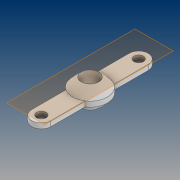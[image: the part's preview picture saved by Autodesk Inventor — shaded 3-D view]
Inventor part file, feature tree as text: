
AUTODESK INVENTOR PART (.ipt)
format: ipt  version: 2021 (Build 250183000, 183)  size: 140,288 bytes
history: native  units: mm
features: sketch x4, extrude x2, plane x1, loft x1, mirror x1
ambient origin geometry x8: Origin, YZ Plane, XZ Plane, XY Plane, X Axis, Y Axis, Z Axis, Center Point
bodies: Solid1 (feature_tree)
feature tree (9):
  extrude  "Extrusion1"  Depth=20.0mm
  plane  "Work Plane1"
  loft  "Loft2"
  extrude  "Extrusion2"  Depth=1.5mm TaperAngle=0.0deg
  mirror  "Mirror1"
  sketch  "Sketch1"  dims[d0=56.0mm d1=20.0mm]
  sketch  "Sketch2"  dims[d2=10.0mm d3=5.5mm]
  sketch  "Sketch3"  dims[d4=5.5mm d5=1.5mm d6=0.0mm]
  sketch  "Sketch4"  dims[d7=5.0mm d12=0.0mm d13=0.0mm d14=0.0mm d15=90.0deg d16=0.0mm d17=90.0deg]
